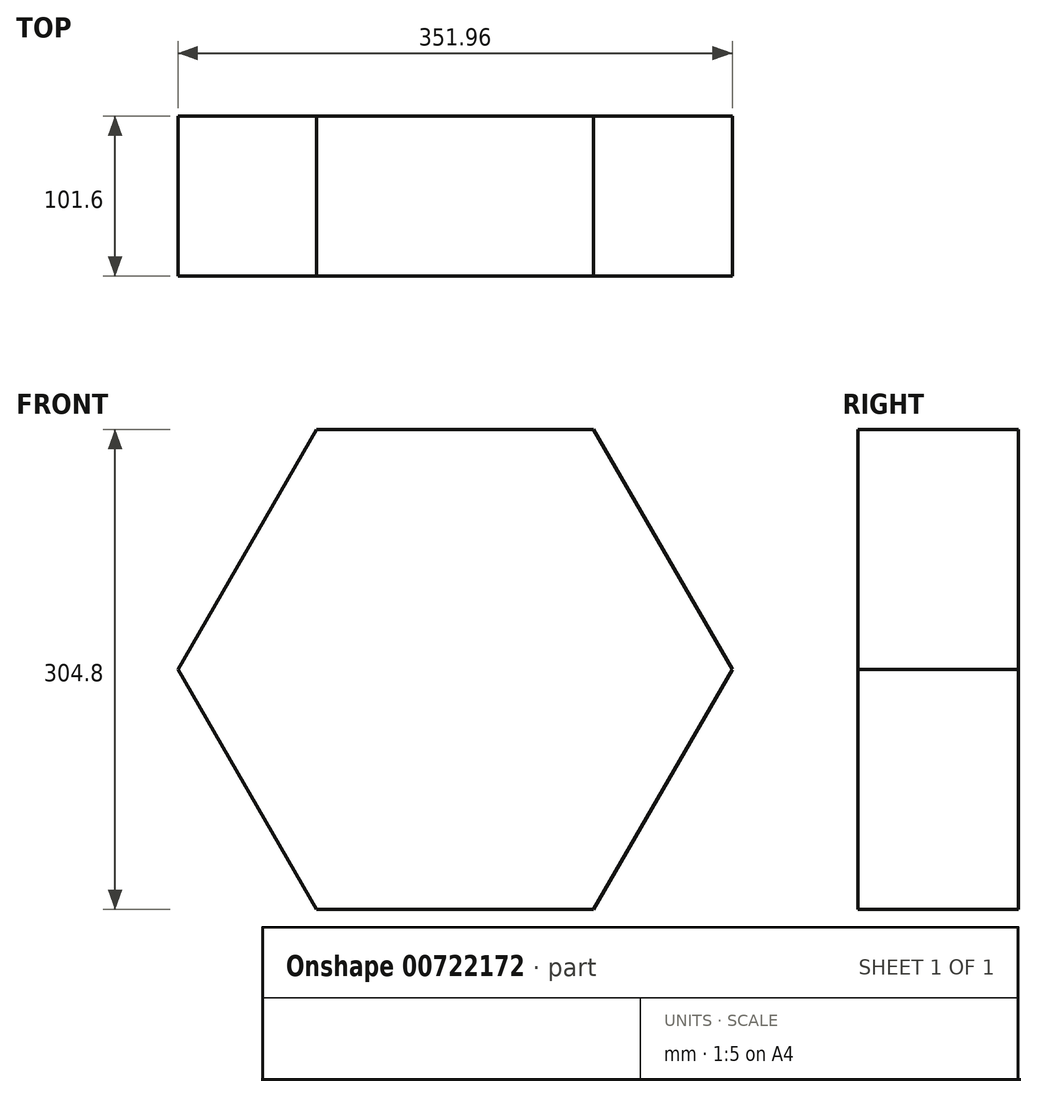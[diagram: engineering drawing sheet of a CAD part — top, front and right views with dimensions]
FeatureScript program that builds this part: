
annotation { "Feature Type Name" : "Feature", "Feature Type Description" : "" }
export const myFeature = defineFeature(function(context is Context, id is Id, definition is map)
    precondition{}
    {
        {
            var Q0;
            Q0=qCreatedBy(makeId("Front.planeOp"),FACE);
            var sketch = newSketch(context, id + "F0", { "sketchPlane" : qUnion([Q0])});
            skCircle(sketch, "E0.cCircle", {"center": v(0, 0) * mm, "radius": 152.4 * mm, "construction": true});
            skLineSegment(sketch, "E0.0", {"start": v(175.98, 0) * mm, "end": v(87.99, -152.4) * mm});
            skLineSegment(sketch, "E0.1", {"start": v(87.99, -152.4) * mm, "end": v(-87.99, -152.4) * mm});
            skLineSegment(sketch, "E0.2", {"start": v(-87.99, -152.4) * mm, "end": v(-175.98, 0) * mm});
            skLineSegment(sketch, "E0.3", {"start": v(-175.98, 0) * mm, "end": v(-87.99, 152.4) * mm});
            skLineSegment(sketch, "E0.4", {"start": v(-87.99, 152.4) * mm, "end": v(87.99, 152.4) * mm});
            skLineSegment(sketch, "E0.5", {"start": v(87.99, 152.4) * mm, "end": v(175.98, 0) * mm});
            skPoint(sketch, "E0.0.midPoint", {"position": v(131.98, -76.2) * mm});
            skSolve(sketch);
        }
        {
            var Q0;
            Q0=qSketchRegion(id+"F0",true);
            extrude(context, id + "F1", {"entities" : qUnion([Q0]), "depth" : 101.6 * mm, "offsetDistance" : 25.4 * mm});
        }
    });
